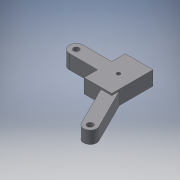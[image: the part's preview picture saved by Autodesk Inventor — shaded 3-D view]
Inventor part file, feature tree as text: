
AUTODESK INVENTOR PART (.ipt)
format: ipt  version: 2017 (Build 210142000, 142)  size: 180,224 bytes
history: native  units: mm
features: extrude x5, sketch x5, projected_geometry x2, plane x1
ambient origin geometry x8: Origin, YZ Plane, XZ Plane, XY Plane, X Axis, Y Axis, Z Axis, Center Point
bodies: Solid1 (feature_tree)
feature tree (13):
  extrude  "Extrusion1"  Depth=19.05mm
  extrude  "Extrusion2"  Depth=10.0mm
  extrude  "Extrusion3"  Depth=10.0mm
  sketch  "Sketch4"  dims[d6=40.0mm d7=15.0mm d8=0.0mm]
  plane  "Work Plane1"
  extrude  "Extrusion4"  Depth=15.0mm TaperAngle=0.0deg
  extrude  "Extrusion5"  Depth=5.0mm
  sketch  "Sketch1"  dims[d0=38.1mm d1=19.05mm]
  sketch  "Sketch2"  dims[d2=10.0mm d3=10.0mm]
  projected_geometry  "Projected Loop1"
  sketch  "Sketch3"  dims[d4=8.0mm d5=10.0mm]
  sketch  "Sketch5"  dims[d9=5.0mm d10=0.0mm d11=5.0mm d12=10.0mm d13=0.0mm d14=80.0mm d15=40.0mm d16=8.5mm d17=10.0mm d18=10.0mm d19=5.0mm d20=10.0mm d21=0.0mm d22=10.0mm d23=0.0mm]
  projected_geometry  "Projected Loop2"
